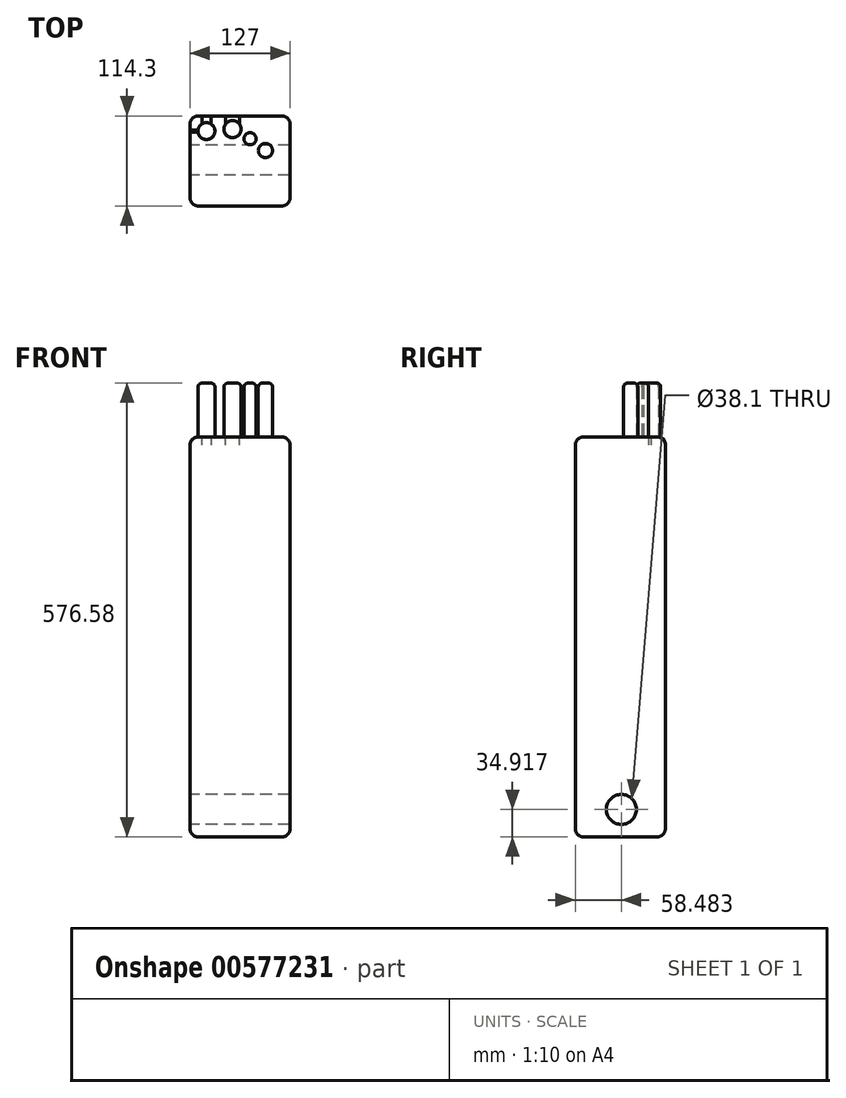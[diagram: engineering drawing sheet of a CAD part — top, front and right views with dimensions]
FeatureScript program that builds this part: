
annotation { "Feature Type Name" : "Feature", "Feature Type Description" : "" }
export const myFeature = defineFeature(function(context is Context, id is Id, definition is map)
    precondition{}
    {
        {
            var Q0;
            Q0=qCreatedBy(makeId("Top.planeOp"),FACE);
            var sketch = newSketch(context, id + "F0", { "sketchPlane" : qUnion([Q0])});
            skLineSegment(sketch, "E0.bottom", {"start": v(-127, 76.37) * mm, "end": v(0, 76.37) * mm});
            skLineSegment(sketch, "E0.top", {"start": v(-127, -37.93) * mm, "end": v(0, -37.93) * mm});
            skLineSegment(sketch, "E0.left", {"start": v(-127, 76.37) * mm, "end": v(-127, -37.93) * mm});
            skLineSegment(sketch, "E0.right", {"start": v(0, 76.37) * mm, "end": v(0, -37.93) * mm});
            skSolve(sketch);
        }
        {
            var Q0;
            Q0=makeQuery(id+"F0.imprint","IMPRINT",FACE,{"disambiguationData":[TD([[makeQuery(id+"F0.imprint","IMPRINT",EDGE,{"derivedFrom":sQuery(id+"F0.wireOp",EDGE,"E0.bottom")}),-1.0]])]});
            extrude(context, id + "F1", {"entities" : qUnion([Q0]), "depth" : 508 * mm, "offsetDistance" : 25.4 * mm});
        }
        {
            var Q0;
            Q0=makeQuery(id+"F1.opExtrude","CAP_FACE",FACE,{"disambiguationData":[OSD([sQuery(id+"F0.wireOp",EDGE,"E0.bottom"),sQuery(id+"F0.wireOp",EDGE,"E0.top"),sQuery(id+"F0.wireOp",EDGE,"E0.left"),sQuery(id+"F0.wireOp",EDGE,"E0.right")])],"isStart":false});
            var sketch = newSketch(context, id + "F2", { "sketchPlane" : qUnion([Q0])});
            skCircle(sketch, "E1", {"center": v(-106.2, 57.21) * mm, "radius": 10.74 * mm});
            skCircle(sketch, "E2", {"center": v(-73.09, 59.65) * mm, "radius": 10.85 * mm});
            skCircle(sketch, "E3", {"center": v(-50.78, 47.45) * mm, "radius": 7.68 * mm});
            skCircle(sketch, "E4", {"center": v(-31.26, 32.47) * mm, "radius": 9.06 * mm});
            skSolve(sketch);
        }
        {
            var Q0;
            Q0 = qSketchRegion(id + "F2", true);
            extrude(context, id + "F3", {"entities" : qUnion([Q0]), "operationType" : NewBodyOperationType.ADD, "depth" : 68.58 * mm, "offsetDistance" : 25.4 * mm});
        }
        {
            var Q0;
            Q0=makeQuery(id+"F3.opExtrude","CAP_EDGE",EDGE,{"disambiguationData":[OSD([sQuery(id+"F2.wireOp",EDGE,"E1")])],"isStart":false});
            var Q1;
            Q1=makeQuery(id+"F3.opExtrude","CAP_EDGE",EDGE,{"disambiguationData":[OSD([sQuery(id+"F2.wireOp",EDGE,"E2")])],"isStart":false});
            var Q2;
            Q2=makeQuery(id+"F3.opExtrude","CAP_EDGE",EDGE,{"disambiguationData":[OSD([sQuery(id+"F2.wireOp",EDGE,"E3")])],"isStart":false});
            var Q3;
            Q3=makeQuery(id+"F3.opExtrude","CAP_EDGE",EDGE,{"disambiguationData":[OSD([sQuery(id+"F2.wireOp",EDGE,"E4")])],"isStart":false});
            fillet(context, id + "F4", {"entities" : qUnion([Q0, Q1, Q2, Q3]), "radius" : 5.08 * mm, "tangentPropagation" : true, "allowEdgeOverflow" : false});
        }
        {
            var Q0;
            Q0=makeQuery(id+"F1.opExtrude","SWEPT_EDGE",EDGE,{"disambiguationData":[OSD([sQuery(id+"F0.wireOp",EDGE,"E0.bottom"),sQuery(id+"F0.wireOp",EDGE,"E0.left")])]});
            var Q1;
            Q1=makeQuery(id+"F1.opExtrude","SWEPT_EDGE",EDGE,{"disambiguationData":[OSD([sQuery(id+"F0.wireOp",EDGE,"E0.top"),sQuery(id+"F0.wireOp",EDGE,"E0.left")])]});
            var Q2;
            Q2=makeQuery(id+"F1.opExtrude","SWEPT_EDGE",EDGE,{"disambiguationData":[OSD([sQuery(id+"F0.wireOp",EDGE,"E0.top"),sQuery(id+"F0.wireOp",EDGE,"E0.right")])]});
            var Q3;
            Q3=makeQuery(id+"F1.opExtrude","SWEPT_EDGE",EDGE,{"disambiguationData":[OSD([sQuery(id+"F0.wireOp",EDGE,"E0.bottom"),sQuery(id+"F0.wireOp",EDGE,"E0.right")])]});
            var Q4;
            Q4=makeQuery(id+"F1.opExtrude","CAP_EDGE",EDGE,{"disambiguationData":[OSD([sQuery(id+"F0.wireOp",EDGE,"E0.right")])],"isStart":true});
            var Q5;
            Q5=makeQuery(id+"F1.opExtrude","CAP_EDGE",EDGE,{"disambiguationData":[OSD([sQuery(id+"F0.wireOp",EDGE,"E0.top")])],"isStart":true});
            var Q6;
            Q6=makeQuery(id+"F1.opExtrude","SWEPT_FACE",FACE,{"disambiguationData":[OSD([sQuery(id+"F0.wireOp",EDGE,"E0.bottom")])]});
            var Q7;
            Q7=makeQuery(id+"F1.opExtrude","CAP_EDGE",EDGE,{"disambiguationData":[OSD([sQuery(id+"F0.wireOp",EDGE,"E0.left")])],"isStart":true});
            fillet(context, id + "F5", {"entities" : qUnion([Q0, Q1, Q2, Q3, Q4, Q5, Q6, Q7]), "radius" : 10.16 * mm, "tangentPropagation" : true, "allowEdgeOverflow" : false});
        }
        {
            var Q0;
            Q0=makeQuery(id+"F1.opExtrude","CAP_EDGE",EDGE,{"disambiguationData":[OSD([sQuery(id+"F0.wireOp",EDGE,"E0.left")])],"isStart":false});
            var Q1;
            Q1=makeQuery(id+"F1.opExtrude","CAP_EDGE",EDGE,{"disambiguationData":[OSD([sQuery(id+"F0.wireOp",EDGE,"E0.top")])],"isStart":false});
            var Q2;
            Q2=makeQuery(id+"F1.opExtrude","CAP_EDGE",EDGE,{"disambiguationData":[OSD([sQuery(id+"F0.wireOp",EDGE,"E0.bottom")])],"isStart":false});
            var Q3;
            Q3=makeQuery(id+"F1.opExtrude","CAP_EDGE",EDGE,{"disambiguationData":[OSD([sQuery(id+"F0.wireOp",EDGE,"E0.right")])],"isStart":false});
            fillet(context, id + "F6", {"entities" : qUnion([Q0, Q1, Q2, Q3]), "radius" : 10.16 * mm, "tangentPropagation" : true, "allowEdgeOverflow" : false});
        }
        {
            var Q0;
            Q0=makeQuery(id+"F1.opExtrude","SWEPT_FACE",FACE,{"disambiguationData":[OSD([sQuery(id+"F0.wireOp",EDGE,"E0.left")])]});
            var sketch = newSketch(context, id + "F7", { "sketchPlane" : qUnion([Q0])});
            skCircle(sketch, "E5", {"center": v(-20.55, 34.92) * mm, "radius": 19.05 * mm});
            skSolve(sketch);
        }
        {
            var Q0;
            Q0=makeQuery(id+"F7.imprint","IMPRINT",FACE,{"disambiguationData":[TD([[makeQuery(id+"F7.imprint","IMPRINT",EDGE,{"derivedFrom":sQuery(id+"F7.wireOp",EDGE,"E5")}),1.0]])]});
            extrude(context, id + "F8", {"entities" : qUnion([Q0]), "operationType" : NewBodyOperationType.REMOVE, "oppositeDirection" : true, "depth" : 127 * mm, "offsetDistance" : 25.4 * mm});
        }
    });
